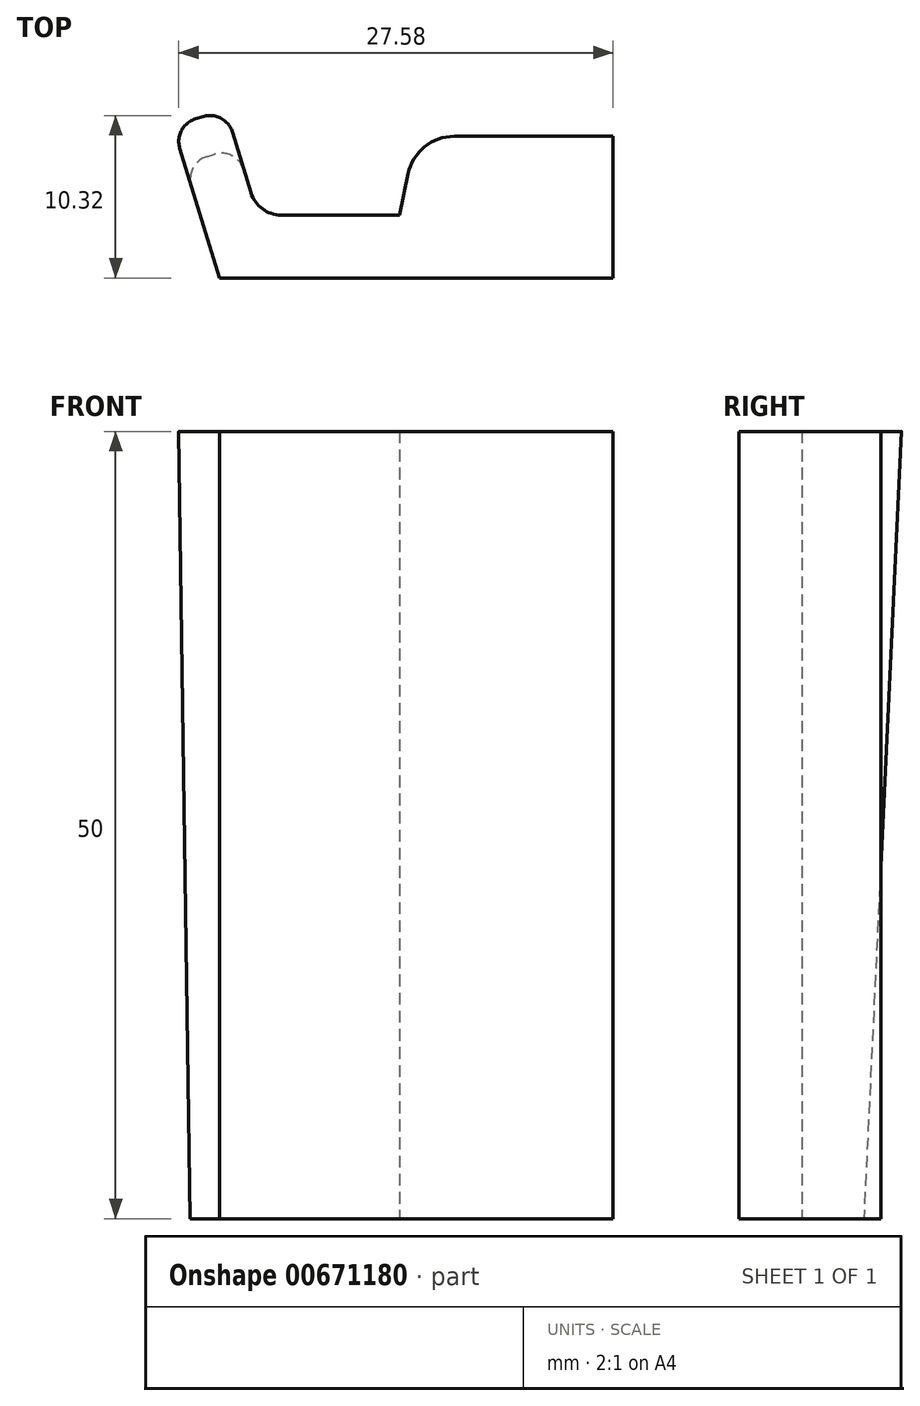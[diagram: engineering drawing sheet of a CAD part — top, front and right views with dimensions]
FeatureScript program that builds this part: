
annotation { "Feature Type Name" : "Feature", "Feature Type Description" : "" }
export const myFeature = defineFeature(function(context is Context, id is Id, definition is map)
    precondition{}
    {
        {
            var Q0;
            Q0=qCreatedBy(makeId("Top.planeOp"),FACE);
            var sketch = newSketch(context, id + "F0", { "sketchPlane" : qUnion([Q0])});
            skLineSegment(sketch, "E0", {"start": v(-7.43, 5.67) * mm, "end": v(-4.47, -4) * mm});
            skLineSegment(sketch, "E1", {"start": v(-4.47, -4) * mm, "end": v(20.53, -4) * mm});
            skLineSegment(sketch, "E2.0", {"start": v(-4.08, 6.7) * mm, "end": v(-2.03, 0) * mm});
            skLineSegment(sketch, "E3", {"start": v(-4.08, 6.7) * mm, "end": v(-7.43, 5.67) * mm});
            skLineSegment(sketch, "E4", {"start": v(6.97, 0) * mm, "end": v(-2.03, 0) * mm});
            skLineSegment(sketch, "E5", {"start": v(20.53, 5) * mm, "end": v(20.53, -4) * mm});
            skLineSegment(sketch, "E6", {"start": v(6.97, 0) * mm, "end": v(8, 5) * mm});
            skLineSegment(sketch, "E7", {"start": v(8, 5) * mm, "end": v(20.53, 5) * mm});
            skPoint(sketch, "E8.orphan", {"position": v(20.53, 0) * mm});
            skPoint(sketch, "E9.orphan", {"position": v(9.05, 10) * mm});
            skSolve(sketch);
        }
        {
            var Q0;
            Q0 = qSketchRegion(id + "F0", true);
            extrude(context, id + "F1", {"entities" : qUnion([Q0]), "depth" : 50 * mm, "offsetDistance" : 25 * mm});
        }
        {
            var Q0;
            Q0=makeQuery(id+"F1.opExtrude","CAP_EDGE",EDGE,{"disambiguationData":[OSD([sQuery(id+"F0.wireOp",EDGE,"E3")])],"isStart":true});
            chamfer(context, id + "F2", {"entities" : qUnion([Q0]), "chamferType" : ChamferType.TWO_OFFSETS, "width1" : 50 * mm, "oppositeDirection" : false, "width2" : 2.5 * mm, "tangentPropagation" : true});
        }
        {
            var Q0;
            Q0=makeQuery(id+"F2.opChamfer","BLEND_EDGE",EDGE,{"blendedFrom":[makeQuery(id+"F1.opExtrude","CAP_EDGE",EDGE,{"disambiguationData":[OSD([sQuery(id+"F0.wireOp",EDGE,"E3")])],"isStart":true}),makeQuery(id+"F1.opExtrude","SWEPT_FACE",FACE,{"disambiguationData":[OSD([sQuery(id+"F0.wireOp",EDGE,"E2.0")])]})],"blendedInto":[makeQuery(id+"F1.opExtrude","SWEPT_FACE",FACE,{"disambiguationData":[OSD([sQuery(id+"F0.wireOp",EDGE,"E2.0")])]})]});
            var Q1;
            Q1=makeQuery(id+"F2.opChamfer","BLEND_EDGE",EDGE,{"blendedFrom":[makeQuery(id+"F1.opExtrude","CAP_EDGE",EDGE,{"disambiguationData":[OSD([sQuery(id+"F0.wireOp",EDGE,"E3")])],"isStart":true}),makeQuery(id+"F1.opExtrude","SWEPT_FACE",FACE,{"disambiguationData":[OSD([sQuery(id+"F0.wireOp",EDGE,"E0")])]})],"blendedInto":[makeQuery(id+"F1.opExtrude","SWEPT_FACE",FACE,{"disambiguationData":[OSD([sQuery(id+"F0.wireOp",EDGE,"E0")])]})]});
            fillet(context, id + "F3", {"entities" : qUnion([Q0, Q1]), "radius" : 1.5 * mm, "tangentPropagation" : true, "allowEdgeOverflow" : false});
        }
        {
            var Q0;
            Q0=makeQuery(id+"F1.opExtrude","SWEPT_EDGE",EDGE,{"disambiguationData":[OSD([sQuery(id+"F0.wireOp",EDGE,"E2.0"),sQuery(id+"F0.wireOp",EDGE,"E4")])]});
            fillet(context, id + "F4", {"entities" : qUnion([Q0]), "radius" : 2 * mm, "tangentPropagation" : true, "allowEdgeOverflow" : false});
        }
        {
            var Q0;
            Q0=makeQuery(id+"F1.opExtrude","SWEPT_EDGE",EDGE,{"disambiguationData":[OSD([sQuery(id+"F0.wireOp",EDGE,"E6"),sQuery(id+"F0.wireOp",EDGE,"E7")])]});
            fillet(context, id + "F5", {"entities" : qUnion([Q0]), "radius" : 3 * mm, "tangentPropagation" : true, "allowEdgeOverflow" : false});
        }
    });
